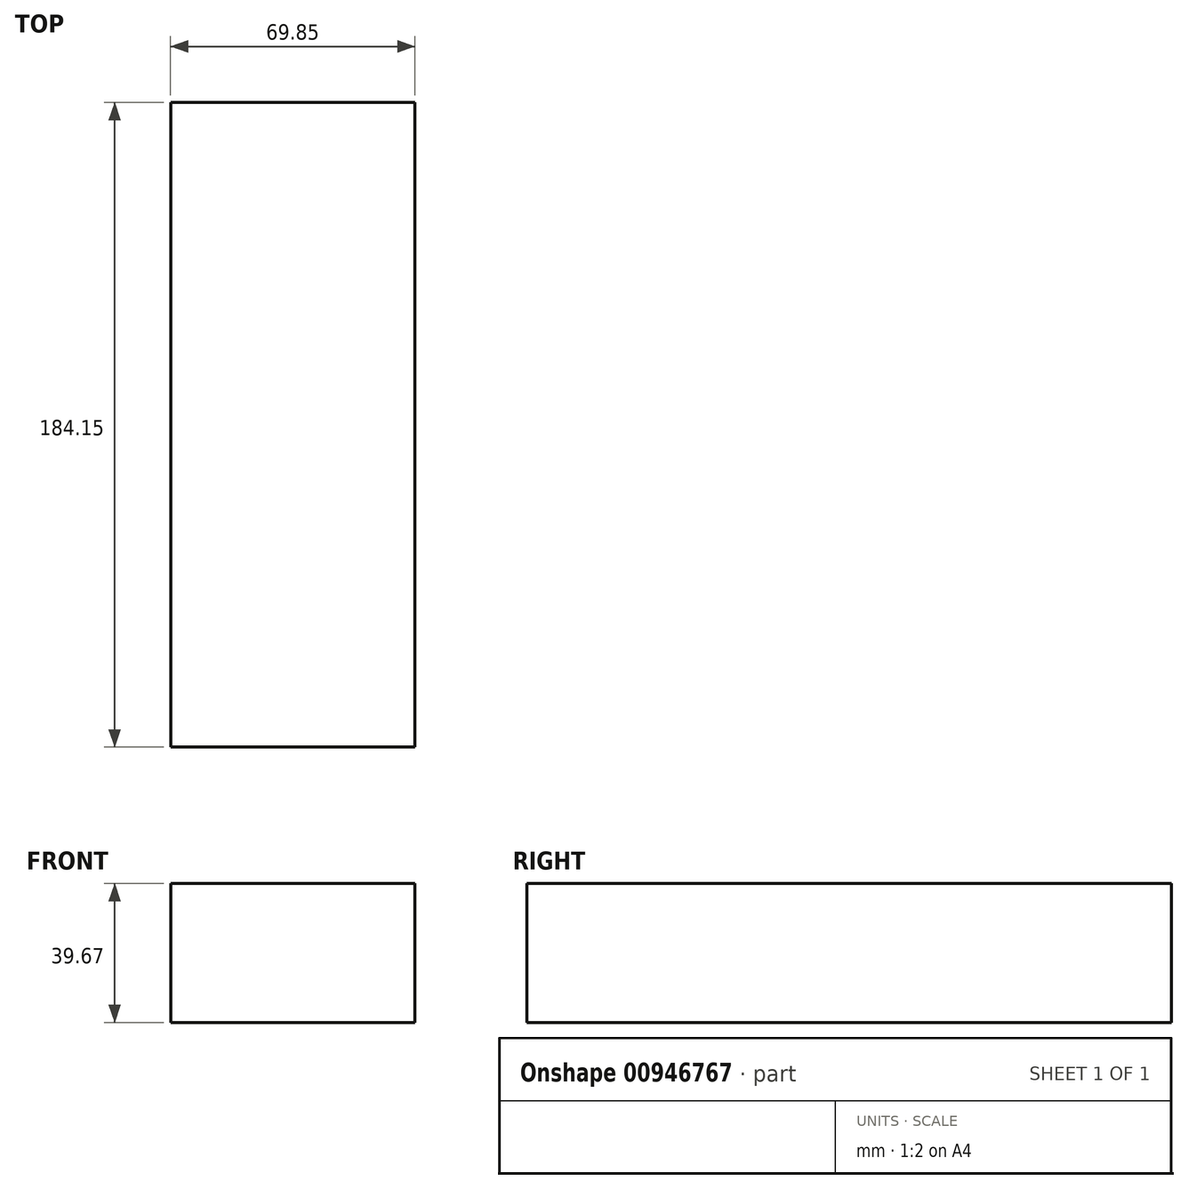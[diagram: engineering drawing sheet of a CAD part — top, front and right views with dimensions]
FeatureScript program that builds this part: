
annotation { "Feature Type Name" : "Feature", "Feature Type Description" : "" }
export const myFeature = defineFeature(function(context is Context, id is Id, definition is map)
    precondition{}
    {
        {
            var Q0;
            Q0=qCreatedBy(makeId("Front.planeOp"),FACE);
            var sketch = newSketch(context, id + "F0", { "sketchPlane" : qUnion([Q0])});
            skLineSegment(sketch, "E0.bottom", {"start": v(-52.15, -32.99) * mm, "end": v(17.7, -32.99) * mm});
            skLineSegment(sketch, "E0.top", {"start": v(-52.15, 6.68) * mm, "end": v(17.7, 6.68) * mm});
            skLineSegment(sketch, "E0.left", {"start": v(-52.15, -32.99) * mm, "end": v(-52.15, 6.68) * mm});
            skLineSegment(sketch, "E0.right", {"start": v(17.7, -32.99) * mm, "end": v(17.7, 6.68) * mm});
            skSolve(sketch);
        }
        {
            var Q0;
            Q0=makeQuery(id+"F0.imprint","IMPRINT",FACE,{"disambiguationData":[TD([[makeQuery(id+"F0.imprint","IMPRINT",EDGE,{"derivedFrom":sQuery(id+"F0.wireOp",EDGE,"E0.bottom")}),1.0]])]});
            extrude(context, id + "F1", {"entities" : qUnion([Q0]), "depth" : 184.15 * mm, "offsetDistance" : 25 * mm});
        }
    });
